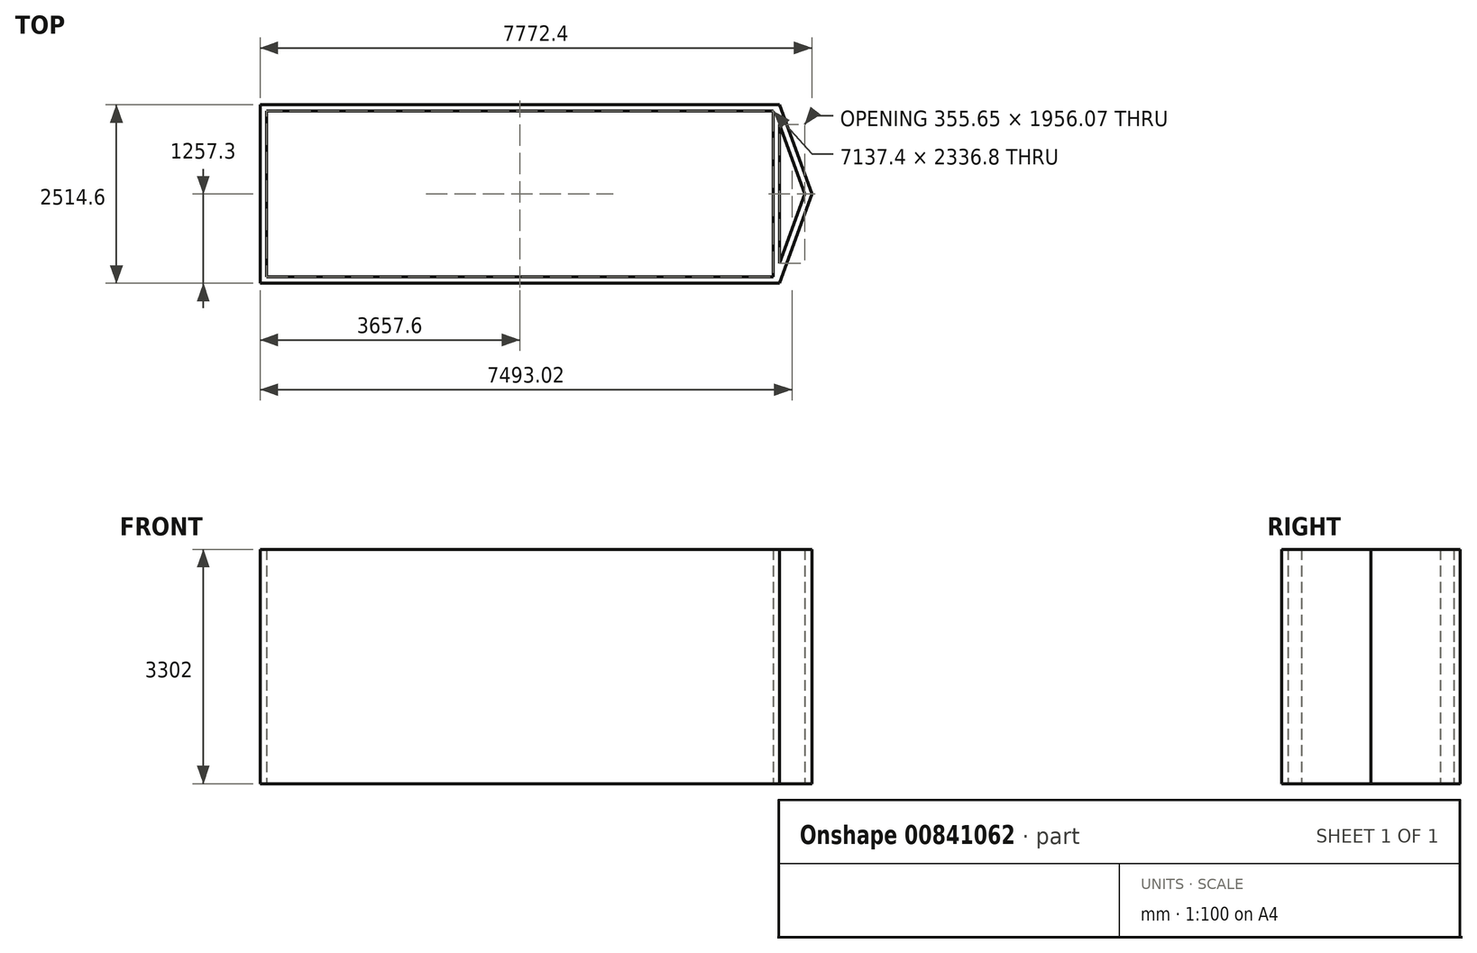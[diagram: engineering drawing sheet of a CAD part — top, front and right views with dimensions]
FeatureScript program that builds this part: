
annotation { "Feature Type Name" : "Feature", "Feature Type Description" : "" }
export const myFeature = defineFeature(function(context is Context, id is Id, definition is map)
    precondition{}
    {
        {
            var Q0;
            Q0=qCreatedBy(makeId("Top.planeOp"),FACE);
            var sketch = newSketch(context, id + "F0", { "sketchPlane" : qUnion([Q0])});
            skLineSegment(sketch, "E0.bottom", {"start": v(-3657.6, 1257.3) * mm, "end": v(3657.6, 1257.3) * mm});
            skLineSegment(sketch, "E0.top", {"start": v(-3657.6, -1257.3) * mm, "end": v(3657.6, -1257.3) * mm});
            skLineSegment(sketch, "E0.left", {"start": v(-3657.6, 1257.3) * mm, "end": v(-3657.6, -1257.3) * mm});
            skLineSegment(sketch, "E0.right", {"start": v(3657.6, 1257.3) * mm, "end": v(3657.6, -1257.3) * mm});
            skPoint(sketch, "E0.middle", {"position": v(0, 0) * mm});
            skLineSegment(sketch, "E1.0", {"start": v(-3568.7, 1168.4) * mm, "end": v(-3568.7, -1168.4) * mm});
            skLineSegment(sketch, "E1.1", {"start": v(-3568.7, 1168.4) * mm, "end": v(3568.7, 1168.4) * mm});
            skLineSegment(sketch, "E1.2", {"start": v(3568.7, 1168.4) * mm, "end": v(3568.7, -1168.4) * mm});
            skLineSegment(sketch, "E1.3", {"start": v(-3568.7, -1168.4) * mm, "end": v(3568.7, -1168.4) * mm});
            skLineSegment(sketch, "E2", {"start": v(3657.6, -1257.3) * mm, "end": v(4114.8, 0) * mm});
            skPoint(sketch, "E2.endSnap0", {"position": v(3657.6, 0) * mm});
            skLineSegment(sketch, "E3", {"start": v(4114.8, 0) * mm, "end": v(3657.6, 1257.3) * mm});
            skLineSegment(sketch, "E4", {"start": v(3657.6, -978.03) * mm, "end": v(4013.25, 0) * mm});
            skLineSegment(sketch, "E5", {"start": v(4013.25, 0) * mm, "end": v(3657.6, 978.03) * mm});
            skSolve(sketch);
        }
        {
            var Q0;
            Q0 = qSketchRegion(id + "F0", true);
            extrude(context, id + "F1", {"entities" : qUnion([Q0]), "depth" : 3302 * mm, "offsetDistance" : 25.4 * mm});
        }
    });
